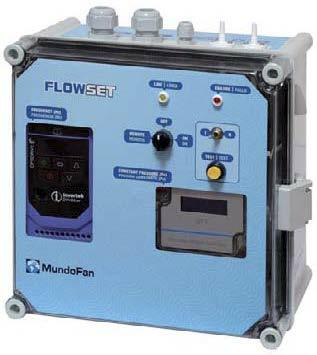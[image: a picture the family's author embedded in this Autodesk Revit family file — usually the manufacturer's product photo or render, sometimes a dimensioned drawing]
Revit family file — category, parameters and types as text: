
# Revit family: FLOWSET-037_VE10839
name_source: partatom
category: Aparatos eléctricos
revit_build: Autodesk Revit 2016 (Build: 20150220_1215(x64)
units: mm (PartAtom-declared; Revit-internal decimal feet)

## family parameters
Compartido = No
Corte con vacíos al cargar = No
Cota de conector redondo = Diámetro de uso
Mantener orientación de anotación = No
Número OmniClass = 23.80.00.00
Punto de cálculo de habitación = No
Se basa en plano de trabajo = No
Siempre vertical = Sí
Tipo de pieza = Caja de conexiones
Título OmniClass = Electric Power and Lighting

## types (1)
- FLOWSET
    Alimentación = 230Vac monofásico
    Corriente = 4,3 A
    Costo = 0 $
    Código de montaje = VE10839
    Descripción = CONTROL EFICIENCIA ENERGETICA PARA VENTILADORES - Caudal aire constante
    Dimensiones máx. = 270x300x170 mm
    Fabricante = SALVADOR ESCODA
    Imagen de tipo = flowset.jpg
    Leds = linea / fallo
    Modelo = FLOWSET 0,37kW
    Normativas = EN-ISO 14644-1:2000
    Potencia = 0,37 kW
    Regulación = Mediante sonda analógica de presión
    Salida = 230Vac monofásico
    Selector = 3 posiciones remoto / off / on
    URL = www.salvadorescoda.com
    Visualización = frecuencia (Hz) y presión (Pa)
